# Revit family: HB-7000SLEMLR
name_source: partatom
category: 衛工裝置
revit_build: Autodesk Revit 2015 (Build: 20140223_1515(x64)
units: mm (PartAtom-declared; Revit-internal decimal feet)

## types (1)
- HB-7000EMLR
    ADA Compliant = X
    Assembly Code = D2010600
    Default Elevation = 0"
    Description = Battery Powered, Sensor Activated, Chrome Plated Brass,4" Centerset Electronic Faucet.
    Finish(es) = CP, PVDPB, PVDBF
    Fixture Color = Not Applicable
    Fixture Material = Chrome Plated
    Flush Volume(s)/Flow Rate(s) = 0.5gpm(1.9 Lpm) Vandal Resistent Spray Head
    Manufacturer = Hydrotek International, Inc.
    Model = HB-7000EMLR
    Mounting = Deck-Mount
    NSF Certification = NSF/ANSI standard 372
    Operation = Sensor-Activated
    P. Plug-in transformer = Not Applicable
    Power Source = Battery Powered
    Price = Prices may vary. Please consult Hydrotek Int'l for most up-to-date price list.
    Product URL = http://www.hydrotekintl.com
    Revised Date = 07/28/2015
    URL = http://www.hydrotekintl.com
    Warranty = 3 Years (Limited)

## geometry (parser evidence)
native form markers: Sweep x3
no freeform markers — native parametric forms only
